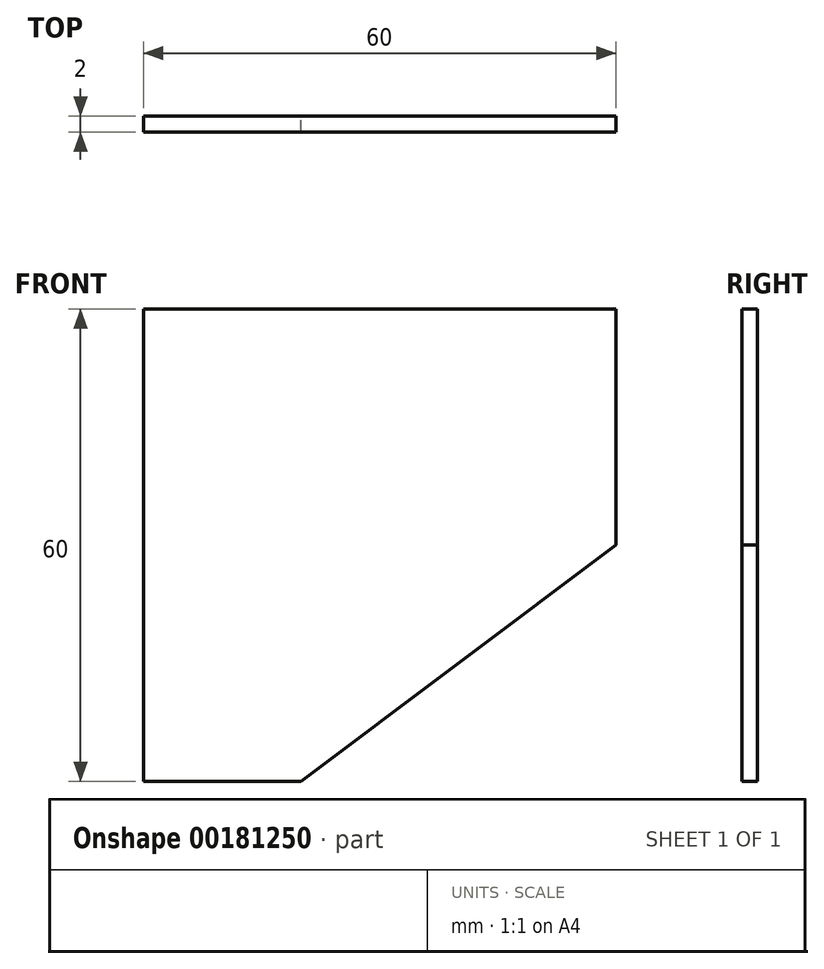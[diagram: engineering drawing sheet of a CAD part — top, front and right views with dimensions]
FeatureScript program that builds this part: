
annotation { "Feature Type Name" : "Feature", "Feature Type Description" : "" }
export const myFeature = defineFeature(function(context is Context, id is Id, definition is map)
    precondition{}
    {
        {
            var Q0;
            Q0=qCreatedBy(makeId("Front.planeOp"),FACE);
            var sketch = newSketch(context, id + "F0", { "sketchPlane" : qUnion([Q0])});
            skLineSegment(sketch, "E0.bottom", {"start": v(30, 30) * mm, "end": v(-30, 30) * mm});
            skLineSegment(sketch, "E0.top", {"start": v(-10, -30) * mm, "end": v(-30, -30) * mm});
            skLineSegment(sketch, "E0.left", {"start": v(30, 30) * mm, "end": v(30, 0) * mm});
            skLineSegment(sketch, "E0.right", {"start": v(-30, 30) * mm, "end": v(-30, -30) * mm});
            skPoint(sketch, "E0.middle", {"position": v(0, 0) * mm});
            skLineSegment(sketch, "E1", {"start": v(30, 0) * mm, "end": v(-10, -30) * mm});
            skPoint(sketch, "E2.orphan", {"position": v(30, -30) * mm});
            skSolve(sketch);
        }
        {
            var Q0;
            Q0=makeQuery(id+"F0.imprint","IMPRINT",FACE,{"disambiguationData":[TD([[makeQuery(id+"F0.imprint","IMPRINT",EDGE,{"derivedFrom":sQuery(id+"F0.wireOp",EDGE,"E0.bottom")}),1.0]])]});
            extrude(context, id + "F1", {"entities" : qUnion([Q0]), "depth" : 2 * mm});
        }
    });
